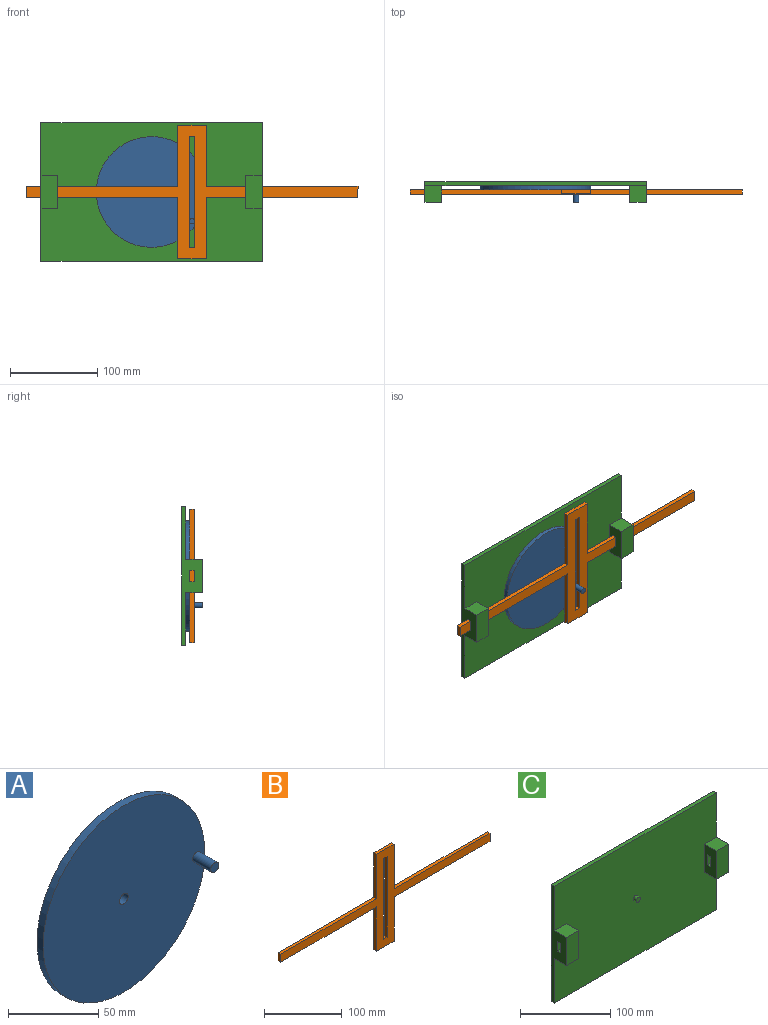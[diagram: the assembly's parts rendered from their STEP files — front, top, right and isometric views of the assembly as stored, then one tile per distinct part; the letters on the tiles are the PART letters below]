
ASSEMBLY  parts=3 mates=3
PART A: 6 faces, bbox 127x19.1x127 mm
  f0: cylinder r=3.37mm len=6.75mm, axis (0,1,0), area 100.9mm2, adj f2,f3
  f1: cylinder r=63.5mm len=127mm, axis (0,1,0), area 1900.2mm2, adj f2,f3
  f2: plane 127x127mm, normal (0,-1,0), area 12600.3mm2, adj f0,f1,f4
  f3: plane 127x127mm, normal (0,1,0), area 12631.9mm2, adj f0,f1
  f4: cylinder r=3.17mm len=14.29mm, axis (0,1,0), area 285mm2, adj f2,f5
  f5: plane 6.35x6.35mm, normal (0,-1,0), area 31.7mm2, adj f4
PART B: 18 faces, bbox 381x4.8x152.8 mm
  f0: plane 6.75x4.76mm, normal (0,0,1), area 32.1mm2, adj f1,f15,f16,f17
  f1: plane 127.4x4.76mm, normal (1,0,0), area 606.7mm2, adj f0,f2,f16,f17
  f2: plane 6.75x4.76mm, normal (0,0,-1), area 32.1mm2, adj f1,f15,f16,f17
  f3: plane 174.43x4.76mm, normal (0,0,-1), area 830.7mm2, adj f4,f14,f16,f17
  f4: plane 12.7x4.76mm, normal (1,0,0), area 60.5mm2, adj f3,f5,f16,f17
  f5: plane 174.43x4.76mm, normal (0,0,1), area 830.7mm2, adj f4,f6,f16,f17
  f6: plane 70.05x4.76mm, normal (1,0,0), area 333.6mm2, adj f5,f7,f16,f17
  f7: plane 32.15x4.76mm, normal (0,0,1), area 153.1mm2, adj f6,f8,f16,f17
  f8: plane 70.05x4.76mm, normal (-1,0,0), area 333.6mm2, adj f7,f9,f16,f17
  f9: plane 174.43x4.76mm, normal (0,0,1), area 830.7mm2, adj f8,f10,f16,f17
  f10: plane 12.7x4.76mm, normal (-1,0,0), area 60.5mm2, adj f9,f11,f16,f17
  f11: plane 174.43x4.76mm, normal (0,0,-1), area 830.7mm2, adj f10,f12,f16,f17
  f12: plane 70.05x4.76mm, normal (-1,0,0), area 333.6mm2, adj f11,f13,f16,f17
  f13: plane 32.15x4.76mm, normal (0,0,-1), area 153.1mm2, adj f12,f14,f16,f17
  f14: plane 70.05x4.76mm, normal (1,0,0), area 333.6mm2, adj f3,f13,f16,f17
  f15: plane 127.4x4.76mm, normal (-1,0,0), area 606.7mm2, adj f0,f2,f16,f17
  f16: plane 381x152.8mm, normal (0,-1,0), area 8482.8mm2, adj f0,f1,f2,f3,f4,f5,f6,f7
  f17: plane 381x152.8mm, normal (0,1,0), area 8482.8mm2, adj f0,f1,f2,f3,f4,f5,f6,f7
PART C: 24 faces, bbox 254x23.8x158.8 mm
  f0: plane 158.75x23.81mm, normal (-1,0,0), area 1416.3mm2, adj f1,f3,f4,f5,f12,f13,f15,f16
  f1: plane 254x4.76mm, normal (0,0,1), area 1209.7mm2, adj f0,f2,f4,f5
  f2: plane 158.75x23.81mm, normal (1,0,0), area 1412.2mm2, adj f1,f3,f4,f5,f8,f10,f11,f20
  f3: plane 254x4.76mm, normal (0,0,-1), area 1209.7mm2, adj f0,f2,f4,f5
  f4: plane 254x158.75mm, normal (0,1,0), area 40322.5mm2, adj f0,f1,f2,f3
  f5: plane 254x158.75mm, normal (0,-1,0), area 38839.2mm2, adj f0,f1,f2,f3,f7,f8,f9,f10
  f6: plane 6.35x6.35mm, normal (0,-1,0), area 31.7mm2, adj f7
  f7: cylinder r=3.17mm len=6.35mm, axis (0,1,0), area 95mm2, adj f5,f6
  f8: plane 19.05x19.05mm, normal (0,0,1), area 362.9mm2, adj f2,f5,f9,f11
  f9: plane 38.1x19.05mm, normal (-1,0,0), area 656.2mm2, adj f5,f8,f10,f11,f20,f21,f22,f23
  f10: plane 19.05x19.05mm, normal (0,0,-1), area 362.9mm2, adj f2,f5,f9,f11
  f11: plane 38.1x19.05mm, normal (0,-1,0), area 725.8mm2, adj f2,f8,f9,f10
  f12: plane 19.05x19.05mm, normal (0,0,1), area 362.9mm2, adj f0,f5,f14,f15
  f13: plane 19.05x19.05mm, normal (0,0,-1), area 362.9mm2, adj f0,f5,f14,f15
  f14: plane 38.1x19.05mm, normal (1,0,0), area 660.3mm2, adj f5,f12,f13,f15,f16,f17,f18,f19
  f15: plane 38.1x19.05mm, normal (0,-1,0), area 725.8mm2, adj f0,f12,f13,f14
  f16: plane 19.05x12.7mm, normal (0,-1,0), area 241.9mm2, adj f0,f14,f18,f19
  f17: plane 19.05x12.7mm, normal (0,1,0), area 241.9mm2, adj f0,f14,f18,f19
  f18: plane 19.05x5.16mm, normal (0,0,1), area 98.3mm2, adj f0,f14,f16,f17
  f19: plane 19.05x5.16mm, normal (0,0,-1), area 98.3mm2, adj f0,f14,f16,f17
  f20: plane 19.05x5.16mm, normal (0,0,1), area 98.3mm2, adj f2,f9,f22,f23
  f21: plane 19.05x5.16mm, normal (0,0,-1), area 98.3mm2, adj f2,f9,f22,f23
  f22: plane 19.05x13.49mm, normal (0,1,0), area 257.1mm2, adj f2,f9,f20,f21
  f23: plane 19.05x13.49mm, normal (0,-1,0), area 257.1mm2, adj f2,f9,f20,f21
PLACE A rot(axis=(0,1,0),35.9deg) t=(-6.14,20.37,-24.33)mm
PLACE B t=(-16.97,20.37,-24.33)mm
PLACE C t=(-6.14,20.37,-24.33)mm fixed
MATE slider B.f4 <-> C.f2  axis (1,0,0) through (230.68,15.61,-24.33)mm
MATE revolute A.f0 <-> C.f7  axis (0,1,0) through (-6.14,15.61,-24.33)mm
MATE pin_slot A.f4 <-> B.f17  axis (0,1,0) through (40.18,15.61,-57.8)mm
